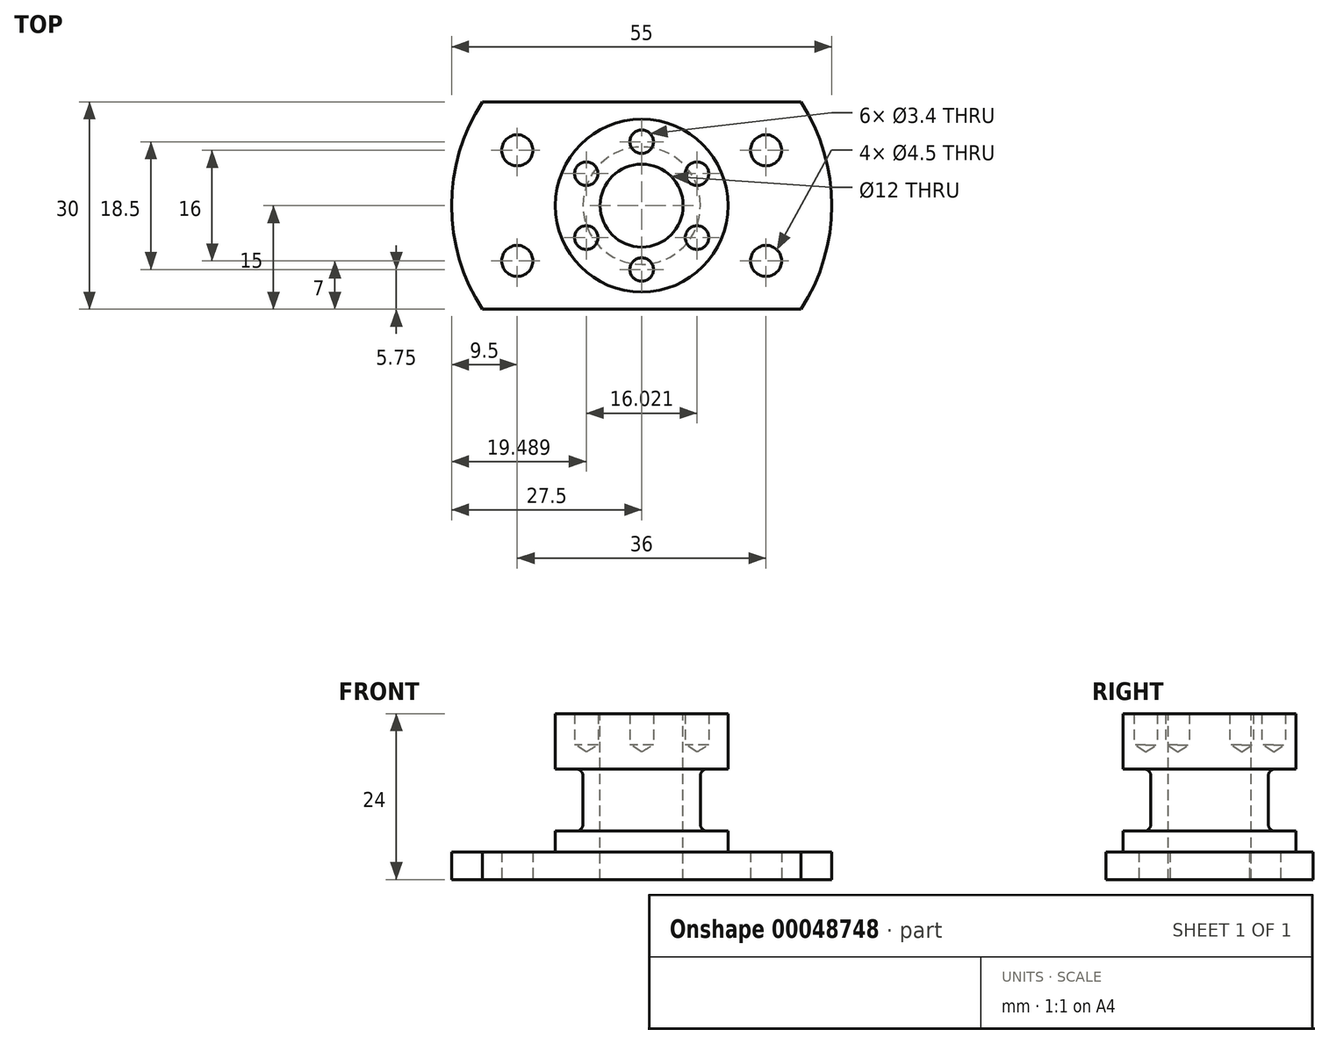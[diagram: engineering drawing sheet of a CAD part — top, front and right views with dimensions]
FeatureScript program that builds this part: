
annotation { "Feature Type Name" : "Feature", "Feature Type Description" : "" }
export const myFeature = defineFeature(function(context is Context, id is Id, definition is map)
    precondition{}
    {
        {
            var Q0;
            Q0=qCreatedBy(makeId("Front.planeOp"),FACE);
            var sketch = newSketch(context, id + "F0", { "sketchPlane" : qUnion([Q0]), "disableImprinting" : false});
            skLineSegment(sketch, "E0", {"start": v(27.5, 0) * mm, "end": v(27.5, 4) * mm});
            skLineSegment(sketch, "E1", {"start": v(8.5, 7) * mm, "end": v(8.5, 16) * mm});
            skLineSegment(sketch, "E2", {"start": v(8.5, 16) * mm, "end": v(12.5, 16) * mm});
            skLineSegment(sketch, "E3", {"start": v(12.5, 16) * mm, "end": v(12.5, 24) * mm});
            skLineSegment(sketch, "E4", {"start": v(12.5, 24) * mm, "end": v(6, 24) * mm});
            skLineSegment(sketch, "E5", {"start": v(6, 24) * mm, "end": v(6, 0) * mm});
            skLineSegment(sketch, "E6", {"start": v(6, 0) * mm, "end": v(27.5, 0) * mm});
            skLineSegment(sketch, "E7", {"start": v(0, 22.1) * mm, "end": v(0, 0) * mm, "construction": true});
            skLineSegment(sketch, "E8", {"start": v(8.5, 7) * mm, "end": v(12.5, 7) * mm});
            skLineSegment(sketch, "E9", {"start": v(12.5, 7) * mm, "end": v(12.5, 4) * mm});
            skLineSegment(sketch, "E10", {"start": v(12.5, 4) * mm, "end": v(27.5, 4) * mm});
            skSolve(sketch);
        }
        {
            var Q0;
            Q0=makeQuery(id+"F0.imprint","IMPRINT",FACE,{"disambiguationData":[TD([[makeQuery(id+"F0.imprint","IMPRINT",EDGE,{"derivedFrom":sQuery(id+"F0.wireOp",EDGE,"E0")}),1.0]])]});
            var Q1;
            Q1=sQuery(id+"F0.wireOp",EDGE,"E7");
            revolve(context, id + "F1", {"surfaceOperationType" : NewSurfaceOperationType.NEW, "entities" : qUnion([Q0]), "axis" : qUnion([Q1]), "revolveType" : RevolveType.FULL});
        }
        {
            var Q0;
            Q0=makeQuery(id+"F1.opRevolve","SWEPT_FACE",FACE,{"disambiguationData":[OSD([sQuery(id+"F0.wireOp",EDGE,"E6")])]});
            var sketch = newSketch(context, id + "F2", { "sketchPlane" : qUnion([Q0])});
            skLineSegment(sketch, "E11.bottom", {"start": v(40, -15) * mm, "end": v(-40, -15) * mm});
            skLineSegment(sketch, "E11.top", {"start": v(40, 15) * mm, "end": v(-40, 15) * mm});
            skLineSegment(sketch, "E11.left", {"start": v(40, -15) * mm, "end": v(40, 15) * mm});
            skLineSegment(sketch, "E11.right", {"start": v(-40, -15) * mm, "end": v(-40, 15) * mm});
            skPoint(sketch, "E11.middle", {"position": v(0, 0) * mm});
            skSolve(sketch);
        }
        {
            var Q0;
            {var subQ0=sQuery(id+"F0.wireOp",EDGE,"E6");Q0=makeQuery(id+"F2.imprint","IMPRINT",FACE,{"disambiguationData":[TD([[makeQuery(id+"F2.imprint","IMPRINT",EDGE,{"derivedFrom":makeQuery(id+"F1.opRevolve","SWEPT_EDGE",EDGE,{"disambiguationData":[OSD([sQuery(id+"F0.wireOp",EDGE,"E5"),subQ0])]})}),1.0]])]});}
            extrude(context, id + "F3", {"entities" : qUnion([Q0]), "operationType" : NewBodyOperationType.INTERSECT, "oppositeDirection" : true, "depth" : 25 * mm, "offsetDistance" : 25 * mm});
        }
        {
            var Q0;
            Q0=makeQuery(id+"F1.opRevolve","SWEPT_EDGE",EDGE,{"disambiguationData":[OSD([sQuery(id+"F0.wireOp",EDGE,"qQLjmfrq-bW2P-8HC8-8tZ1-FgJvKszlCRau"),sQuery(id+"F0.wireOp",EDGE,"E1")])]});
            var Q1;
            Q1=makeQuery(id+"F1.opRevolve","SWEPT_EDGE",EDGE,{"disambiguationData":[OSD([sQuery(id+"F0.wireOp",EDGE,"E1"),sQuery(id+"F0.wireOp",EDGE,"E2")])]});
            fillet(context, id + "F4", {"entities" : qUnion([Q0, Q1]), "tangentPropagation" : true, "blendControlType" : BlendControlType.RADIUS, "radius" : 1 * mm, "width" : 5 * mm, "defaultsChanged" : false, "isAsymmetric" : false, "otherRadius" : 5 * mm, "flipAsymmetric" : false, "isPartial" : false, "partialFirstEdgeTotalParameter" : 0.01, "partialOppositeParameter" : true, "secondBound" : false, "partialSecondEdgeTotalParameter" : 0.99, "vertexSettings" : [], "pointOnEdgeSettings" : [], "allowEdgeOverflow" : false, "smoothCorners" : false, "filletType" : FilletType.EDGE});
        }
        {
            var Q0;
            Q0=makeQuery(id+"F1.opRevolve","SWEPT_FACE",FACE,{"disambiguationData":[OSD([sQuery(id+"F0.wireOp",EDGE,"E4")])]});
            var sketch = newSketch(context, id + "F5", { "sketchPlane" : qUnion([Q0])});
            skPoint(sketch, "E12", {"position": v(0, 9.25) * mm});
            skPoint(sketch, "E13.1.0", {"position": v(-8.01, 4.63) * mm});
            skPoint(sketch, "E13.2.0", {"position": v(-8.01, -4.62) * mm});
            skPoint(sketch, "E13.3.0", {"position": v(0, -9.25) * mm});
            skPoint(sketch, "E13.4.0", {"position": v(8.01, -4.63) * mm});
            skPoint(sketch, "E13.5.0", {"position": v(8.01, 4.63) * mm});
            skPoint(sketch, "E13.center", {"position": v(0, 0) * mm});
            skSolve(sketch);
        }
        {
            var Q0;
            Q0=sQuery(id+"F5.wireOp",VERTEX,"E12");
            var Q1;
            Q1=sQuery(id+"F5.wireOp",VERTEX,"E13.5.0");
            var Q2;
            Q2=sQuery(id+"F5.wireOp",VERTEX,"E13.4.0");
            var Q3;
            Q3=sQuery(id+"F5.wireOp",VERTEX,"E13.3.0");
            var Q4;
            Q4=sQuery(id+"F5.wireOp",VERTEX,"E13.2.0");
            var Q5;
            Q5=sQuery(id+"F5.wireOp",VERTEX,"E13.1.0");
            var Q6;
            Q6=makeQuery(id+"F1.opRevolve","SWEPT_BODY",BODY,{"disambiguationData":[OSD([sQuery(id+"F0.wireOp",EDGE,"E0"),sQuery(id+"F0.wireOp",EDGE,"DLiDpo88-2T5Z-tGUK-vVsQ-TvNKD2erqAq3"),sQuery(id+"F0.wireOp",EDGE,"6BENFza0-CuJM-OG8z-Jko5-KcAo7BCyaul2"),sQuery(id+"F0.wireOp",EDGE,"qQLjmfrq-bW2P-8HC8-8tZ1-FgJvKszlCRau"),sQuery(id+"F0.wireOp",EDGE,"E1"),sQuery(id+"F0.wireOp",EDGE,"E2"),sQuery(id+"F0.wireOp",EDGE,"E3"),sQuery(id+"F0.wireOp",EDGE,"E4"),sQuery(id+"F0.wireOp",EDGE,"E5"),sQuery(id+"F0.wireOp",EDGE,"E6")])]});
            hole(context, id + "F6", {"style" : HoleStyle.SIMPLE, "endStyle" : HoleEndStyle.BLIND, "standardTappedOrClearance" : lookupTablePath({ "fit" : "Normal", "standard" : "ISO", "size" : "M3", "type" : "Clearance" }), "standardBlindInLast" : lookupTablePath({ "fit" : "Normal", "standard" : "ISO", "engagement" : "75%", "pitch" : "0.5 mm", "size" : "M3", "type" : "Clearance & tapped" }), "holeDiameter" : 3.4 * mm, "majorDiameter" : 3 * mm, "holeDepth" : 4.5 * mm, "isTappedThrough" : true, "tappedDepth" : 3 * mm, "tapClearance" : 3, "locations" : qUnion([Q0, Q1, Q2, Q3, Q4, Q5]), "scope" : qUnion([Q6]), "startStyle" : HoleStartStyle.PART});
        }
        {
            var Q0;
            Q0=makeQuery(id+"F1.opRevolve","SWEPT_FACE",FACE,{"disambiguationData":[OSD([sQuery(id+"F0.wireOp",EDGE,"E10")])]});
            var sketch = newSketch(context, id + "F7", { "sketchPlane" : qUnion([Q0])});
            skPoint(sketch, "E14", {"position": v(-18, 8) * mm});
            skPoint(sketch, "E15.0.1.0", {"position": v(-18, -8) * mm});
            skPoint(sketch, "E15.1.0.0", {"position": v(18, 8) * mm});
            skPoint(sketch, "E15.1.1.0", {"position": v(18, -8) * mm});
            skLineSegment(sketch, "E15.direction1", {"start": v(-18, 8) * mm, "end": v(18, 8) * mm, "construction": true});
            skLineSegment(sketch, "E15.direction2", {"start": v(-18, 8) * mm, "end": v(-18, -8) * mm, "construction": true});
            skSolve(sketch);
        }
        {
            var Q0;
            Q0=sQuery(id+"F7.wireOp",VERTEX,"0e9d7b8a-8adb-4bb3-a86e-9f6fb4a7c859.2.0");
            var Q1;
            Q1=sQuery(id+"F7.wireOp",VERTEX,"0e9d7b8a-8adb-4bb3-a86e-9f6fb4a7c859.3.0");
            var Q2;
            Q2=sQuery(id+"F7.wireOp",VERTEX,"0e9d7b8a-8adb-4bb3-a86e-9f6fb4a7c859.8.0");
            var Q3;
            Q3=sQuery(id+"F7.wireOp",VERTEX,"0e9d7b8a-8adb-4bb3-a86e-9f6fb4a7c859.7.0");
            var Q4;
            Q4=sQuery(id+"F7.wireOp",VERTEX,"E14");
            var Q5;
            Q5=sQuery(id+"F7.wireOp",VERTEX,"E15.0.1.0");
            var Q6;
            Q6=sQuery(id+"F7.wireOp",VERTEX,"E15.1.0.0");
            var Q7;
            Q7=sQuery(id+"F7.wireOp",VERTEX,"E15.1.1.0");
            var Q8;
            Q8=makeQuery(id+"F1.opRevolve","SWEPT_BODY",BODY,{"disambiguationData":[OSD([sQuery(id+"F0.wireOp",EDGE,"E0"),sQuery(id+"F0.wireOp",EDGE,"DLiDpo88-2T5Z-tGUK-vVsQ-TvNKD2erqAq3"),sQuery(id+"F0.wireOp",EDGE,"6BENFza0-CuJM-OG8z-Jko5-KcAo7BCyaul2"),sQuery(id+"F0.wireOp",EDGE,"qQLjmfrq-bW2P-8HC8-8tZ1-FgJvKszlCRau"),sQuery(id+"F0.wireOp",EDGE,"E1"),sQuery(id+"F0.wireOp",EDGE,"E2"),sQuery(id+"F0.wireOp",EDGE,"E3"),sQuery(id+"F0.wireOp",EDGE,"E4"),sQuery(id+"F0.wireOp",EDGE,"E5"),sQuery(id+"F0.wireOp",EDGE,"E6")])]});
            hole(context, id + "F8", {"style" : HoleStyle.SIMPLE, "endStyle" : HoleEndStyle.BLIND, "standardTappedOrClearance" : lookupTablePath({ "fit" : "Normal", "standard" : "ISO", "size" : "M4", "type" : "Clearance" }), "standardBlindInLast" : lookupTablePath({ "fit" : "Normal", "standard" : "ISO", "engagement" : "75%", "pitch" : "0.7 mm", "size" : "M4", "type" : "Clearance & tapped" }), "holeDiameter" : 4.5 * mm, "majorDiameter" : 5 * mm, "holeDepth" : 4.5 * mm, "isTappedThrough" : true, "tappedDepth" : 3 * mm, "tapClearance" : 3, "locations" : qUnion([Q0, Q1, Q2, Q3, Q4, Q5, Q6, Q7]), "scope" : qUnion([Q8]), "startStyle" : HoleStartStyle.PART});
        }
    });
